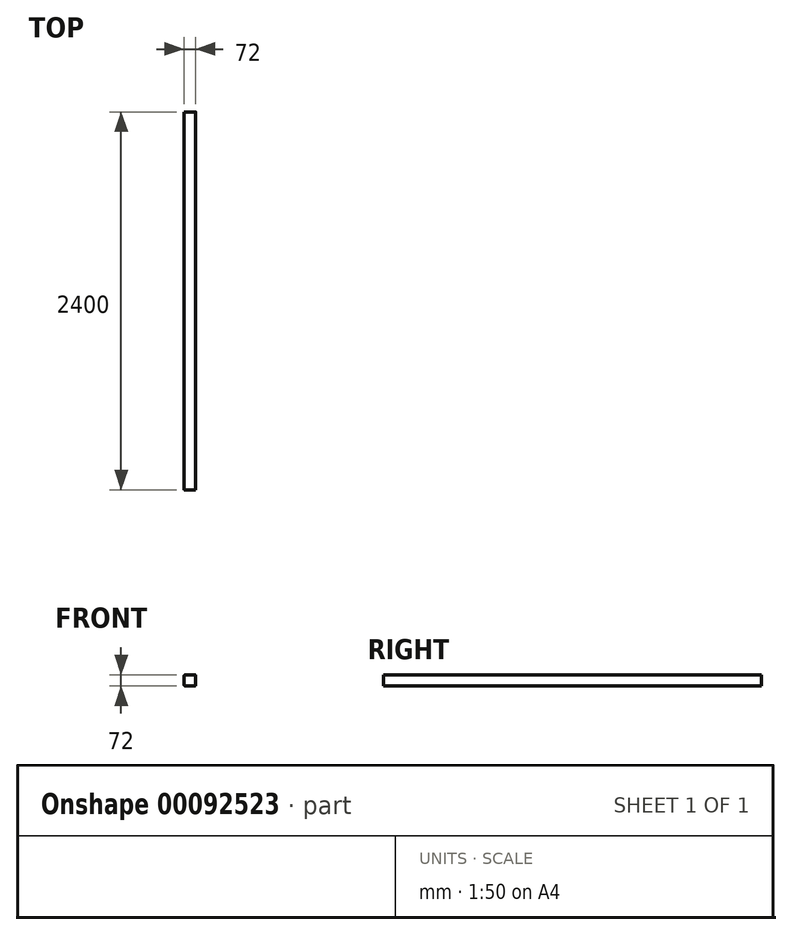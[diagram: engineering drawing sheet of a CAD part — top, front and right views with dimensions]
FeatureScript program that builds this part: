
annotation { "Feature Type Name" : "Feature", "Feature Type Description" : "" }
export const myFeature = defineFeature(function(context is Context, id is Id, definition is map)
    precondition{}
    {
        {
            var Q0;
            Q0=qCreatedBy(makeId("Front.planeOp"),FACE);
            var sketch = newSketch(context, id + "F0", { "sketchPlane" : qUnion([Q0])});
            skLineSegment(sketch, "E0.bottom", {"start": v(31, 36) * mm, "end": v(-31, 36) * mm});
            skLineSegment(sketch, "E0.top", {"start": v(31, -36) * mm, "end": v(-31, -36) * mm});
            skLineSegment(sketch, "E0.left", {"start": v(36, 31) * mm, "end": v(36, -31) * mm});
            skLineSegment(sketch, "E0.right", {"start": v(-36, 31) * mm, "end": v(-36, -31) * mm});
            skPoint(sketch, "E0.middle", {"position": v(0, 0) * mm});
            skPoint(sketch, "E1.visualSharp", {"position": v(-36, 36) * mm});
            skArc(sketch, "E1.filletArc", {"start": v(-31, 36) * mm, "mid": v(-34.54, 34.54) * mm, "end": v(-36, 31) * mm});
            skPoint(sketch, "E2.visualSharp", {"position": v(36, 36) * mm});
            skPoint(sketch, "E3.visualSharp", {"position": v(36, -36) * mm});
            skArc(sketch, "E3.filletArc", {"start": v(31, -36) * mm, "mid": v(34.54, -34.54) * mm, "end": v(36, -31) * mm});
            skPoint(sketch, "E4.visualSharp", {"position": v(-36, -36) * mm});
            skArc(sketch, "E4.filletArc", {"start": v(-36, -31) * mm, "mid": v(-34.54, -34.54) * mm, "end": v(-31, -36) * mm});
            skArc(sketch, "E5.filletArc", {"start": v(36, 31) * mm, "mid": v(34.54, 34.54) * mm, "end": v(31, 36) * mm});
            skSolve(sketch);
        }
        {
            var Q0;
            Q0=qSketchRegion(id+"F0",true);
            extrude(context, id + "F1", {"entities" : qUnion([Q0]), "depth" : 2400 * mm});
        }
    });
